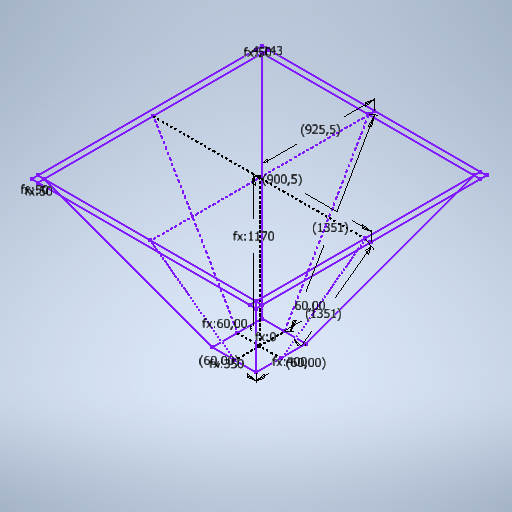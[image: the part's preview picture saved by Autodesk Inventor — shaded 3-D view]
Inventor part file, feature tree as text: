
AUTODESK INVENTOR PART (.ipt)
format: ipt  version: 2025 (Build 290162010, 162A)  size: 305,152 bytes
history: native  units: in
note: dims shown in document units (in); Inventor stores cm internally (conversion verified against a paired STEP export)
features: sketch x2
ambient origin geometry x8: Origin, YZ Plane, XZ Plane, XY Plane, X Axis, Y Axis, Z Axis, Center Point
feature tree (2):
  sketch  "Sketch3"  dims[d16=0.0in d17=15.748in d18=13.7795in d22=0.4188in d23=0.4124in d36=1.9685in d37=1.9685in d38=1.9685in d39=36.437in d41=35.4527in d42=0.1631in d43=53.189in d44=53.189in d46=46.063in d47=60.0deg d48=60.0deg d49=60.0deg d50=60.0deg]
  sketch  "3D Sketch3"
